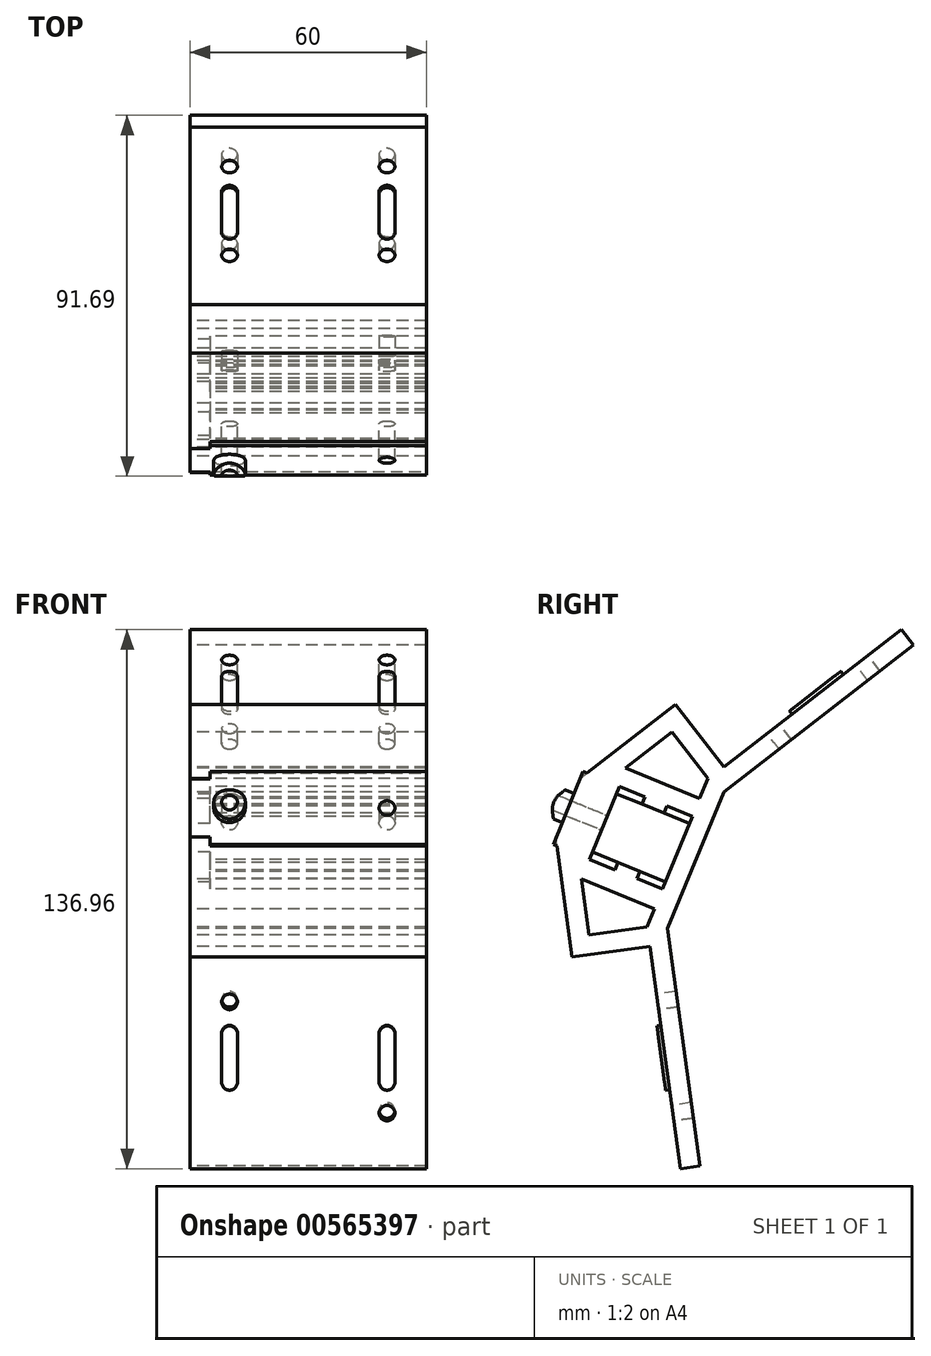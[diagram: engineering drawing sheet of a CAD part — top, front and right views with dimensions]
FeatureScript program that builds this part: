
annotation { "Feature Type Name" : "Feature", "Feature Type Description" : "" }
export const myFeature = defineFeature(function(context is Context, id is Id, definition is map)
    precondition{}
    {
        {
            var Q0;
            Q0=qCreatedBy(makeId("Right.planeOp"),FACE);
            var sketch = newSketch(context, id + "F0", { "sketchPlane" : qUnion([Q0])});
            skLineSegment(sketch, "E0", {"start": v(-33.6, 14.18) * mm, "end": v(-1.95, 38.65) * mm});
            skLineSegment(sketch, "E1", {"start": v(-1.95, 38.65) * mm, "end": v(10.28, 22.83) * mm});
            skLineSegment(sketch, "E2", {"start": v(-8.4, -22.77) * mm, "end": v(-28.23, -25.46) * mm});
            skLineSegment(sketch, "E3", {"start": v(-28.23, -25.46) * mm, "end": v(-33.6, 14.18) * mm});
            skLineSegment(sketch, "E4", {"start": v(10.28, 22.83) * mm, "end": v(55.37, 57.7) * mm});
            skLineSegment(sketch, "E5", {"start": v(55.37, 57.7) * mm, "end": v(58.43, 53.74) * mm});
            skLineSegment(sketch, "E6", {"start": v(58.43, 53.74) * mm, "end": v(10.28, 16.5) * mm});
            skLineSegment(sketch, "E7", {"start": v(10.28, 16.5) * mm, "end": v(-3.97, -18.27) * mm});
            skLineSegment(sketch, "E8", {"start": v(-3.97, -18.27) * mm, "end": v(4.2, -78.59) * mm});
            skLineSegment(sketch, "E9", {"start": v(4.2, -78.59) * mm, "end": v(-0.75, -79.26) * mm});
            skLineSegment(sketch, "E10", {"start": v(-0.75, -79.26) * mm, "end": v(-8.4, -22.77) * mm});
            skPoint(sketch, "E11", {"position": v(34.35, 35.12) * mm});
            skPoint(sketch, "E12", {"position": v(0.11, -48.43) * mm});
            skLineSegment(sketch, "E13", {"start": v(2.32, 10.27) * mm, "end": v(-16.19, 17.85) * mm});
            skLineSegment(sketch, "E14", {"start": v(-16.19, 17.85) * mm, "end": v(-23.77, -0.65) * mm});
            skLineSegment(sketch, "E15", {"start": v(-23.77, -0.65) * mm, "end": v(-5.26, -8.24) * mm});
            skLineSegment(sketch, "E16", {"start": v(-5.26, -8.24) * mm, "end": v(2.32, 10.27) * mm});
            skPoint(sketch, "E17", {"position": v(3.15, -0.88) * mm});
            skPoint(sketch, "E18", {"position": v(-1.47, 1.01) * mm});
            skLineSegment(sketch, "E19", {"start": v(3.15, -0.88) * mm, "end": v(-1.47, 1.01) * mm});
            skLineSegment(sketch, "E20", {"start": v(1.56, 8.42) * mm, "end": v(-16.94, 16) * mm});
            skLineSegment(sketch, "E21", {"start": v(-4.5, -6.39) * mm, "end": v(-23.01, 1.2) * mm});
            skLineSegment(sketch, "E22", {"start": v(-11.74, -5.58) * mm, "end": v(-10.98, -3.73) * mm});
            skLineSegment(sketch, "E23", {"start": v(-17.3, -3.3) * mm, "end": v(-16.53, -1.46) * mm});
            skLineSegment(sketch, "E24", {"start": v(-10.47, 13.35) * mm, "end": v(-9.7, 15.2) * mm});
            skPoint(sketch, "E25", {"position": v(-14.52, -4.45) * mm});
            skPoint(sketch, "E26", {"position": v(-6.93, 14.06) * mm});
            skLineSegment(sketch, "E27", {"start": v(-4.92, 11.07) * mm, "end": v(-4.16, 12.92) * mm});
            skLineSegment(sketch, "E28", {"start": v(-2.85, 31.63) * mm, "end": v(6.25, 19.86) * mm});
            skLineSegment(sketch, "E29", {"start": v(6.25, 19.86) * mm, "end": v(4.17, 14.8) * mm});
            skLineSegment(sketch, "E30", {"start": v(4.17, 14.8) * mm, "end": v(-14.65, 22.5) * mm});
            skLineSegment(sketch, "E31", {"start": v(-14.65, 22.5) * mm, "end": v(-2.85, 31.63) * mm});
            skLineSegment(sketch, "E32", {"start": v(-7.31, -13.24) * mm, "end": v(-9.2, -17.83) * mm});
            skLineSegment(sketch, "E33", {"start": v(-9.2, -17.83) * mm, "end": v(-23.94, -19.83) * mm});
            skLineSegment(sketch, "E34", {"start": v(-23.94, -19.83) * mm, "end": v(-25.87, -5.64) * mm});
            skPoint(sketch, "E34.endSnap0", {"position": v(-30.91, -5.64) * mm});
            skLineSegment(sketch, "E35", {"start": v(-25.87, -5.64) * mm, "end": v(-7.31, -13.24) * mm});
            skSolve(sketch);
        }
        {
            var Q0;
            Q0 = qSketchRegion(id + "F0", true);
            extrude(context, id + "F1", {"entities" : qUnion([Q0]), "depth" : 60 * mm, "offsetDistance" : 25 * mm});
        }
        {
            var Q0;
            {var subQ3=sQuery(id+"F0.wireOp",EDGE,"E24");Q0=makeQuery(id+"F0.imprint","IMPRINT",FACE,{"disambiguationData":[TD([[makeQuery(id+"F0.imprint","IMPRINT",EDGE,{"derivedFrom":subQ3}),1.0]])]});}
            var Q1;
            {var subQ3=sQuery(id+"F0.wireOp",EDGE,"E27");Q1=makeQuery(id+"F0.imprint","IMPRINT",FACE,{"disambiguationData":[TD([[makeQuery(id+"F0.imprint","IMPRINT",EDGE,{"derivedFrom":subQ3}),-1.0]])]});}
            var Q2;
            {var subQ3=sQuery(id+"F0.wireOp",EDGE,"E22");Q2=makeQuery(id+"F0.imprint","IMPRINT",FACE,{"disambiguationData":[TD([[makeQuery(id+"F0.imprint","IMPRINT",EDGE,{"derivedFrom":subQ3}),-1.0]])]});}
            var Q3;
            {var subQ5=sQuery(id+"F0.wireOp",EDGE,"E23");Q3=makeQuery(id+"F0.imprint","IMPRINT",FACE,{"disambiguationData":[TD([[makeQuery(id+"F0.imprint","IMPRINT",EDGE,{"derivedFrom":subQ5}),1.0]])]});}
            extrude(context, id + "F2", {"entities" : qUnion([Q0, Q1, Q2, Q3]), "operationType" : NewBodyOperationType.ADD, "depth" : 5 * mm, "offsetDistance" : 25 * mm});
        }
        {
            var Q0;
            {var subQ0=sQuery(id+"F0.wireOp",EDGE,"E22");Q0=makeQuery(id+"F0.imprint","IMPRINT",FACE,{"disambiguationData":[TD([[makeQuery(id+"F0.imprint","IMPRINT",EDGE,{"derivedFrom":subQ0}),1.0]])]});}
            var Q1;
            {var subQ0=sQuery(id+"F0.wireOp",EDGE,"E24");Q1=makeQuery(id+"F0.imprint","IMPRINT",FACE,{"disambiguationData":[TD([[makeQuery(id+"F0.imprint","IMPRINT",EDGE,{"derivedFrom":subQ0}),-1.0]])]});}
            extrude(context, id + "F3", {"entities" : qUnion([Q0, Q1]), "operationType" : NewBodyOperationType.ADD, "depth" : 60 * mm, "offsetDistance" : 25 * mm});
        }
        {
            var Q0;
            Q0=makeQuery(id+"F1.opExtrude","SWEPT_EDGE",EDGE,{"disambiguationData":[OSD([sQuery(id+"F0.wireOp",EDGE,"E0"),sQuery(id+"F0.wireOp",EDGE,"E3")])]});
            fillet(context, id + "F4", {"entities" : qUnion([Q0]), "radius" : 5 * mm, "tangentPropagation" : true, "allowEdgeOverflow" : false});
        }
        {
            var Q0;
            Q0=makeQuery(id+"F1.opExtrude","SWEPT_FACE",FACE,{"disambiguationData":[OSD([sQuery(id+"F0.wireOp",EDGE,"E4")])]});
            var sketch = newSketch(context, id + "F5", { "sketchPlane" : qUnion([Q0])});
            skCircle(sketch, "E36", {"center": v(50, 66.47) * mm, "radius": 2 * mm});
            skCircle(sketch, "E37", {"center": v(50, 37.97) * mm, "radius": 2 * mm});
            skCircle(sketch, "E38", {"center": v(10, 37.97) * mm, "radius": 2 * mm});
            skCircle(sketch, "E39", {"center": v(10, 66.47) * mm, "radius": 2 * mm});
            skLineSegment(sketch, "E40", {"start": v(48, 66.47) * mm, "end": v(48, 37.97) * mm});
            skLineSegment(sketch, "E41", {"start": v(12, 37.97) * mm, "end": v(12, 66.47) * mm});
            skLineSegment(sketch, "E42", {"start": v(52, 66.47) * mm, "end": v(52, 37.97) * mm});
            skLineSegment(sketch, "E43", {"start": v(8, 66.47) * mm, "end": v(8, 37.97) * mm});
            skCircle(sketch, "E44", {"center": v(50, 58.47) * mm, "radius": 2 * mm});
            skCircle(sketch, "E45", {"center": v(50, 45.97) * mm, "radius": 2 * mm});
            skCircle(sketch, "E46", {"center": v(10, 58.47) * mm, "radius": 2 * mm});
            skCircle(sketch, "E47", {"center": v(10, 45.97) * mm, "radius": 2 * mm});
            skSolve(sketch);
        }
        {
            var Q0;
            Q0=makeQuery(id+"F1.opExtrude","SWEPT_FACE",FACE,{"disambiguationData":[OSD([sQuery(id+"F0.wireOp",EDGE,"E10")])]});
            var sketch = newSketch(context, id + "F6", { "sketchPlane" : qUnion([Q0])});
            skCircle(sketch, "E48", {"center": v(10, -64.19) * mm, "radius": 2 * mm});
            skCircle(sketch, "E49", {"center": v(10, -35.69) * mm, "radius": 2 * mm});
            skCircle(sketch, "E50", {"center": v(50, -35.7) * mm, "radius": 2 * mm});
            skCircle(sketch, "E51", {"center": v(50, -64.18) * mm, "radius": 2 * mm});
            skLineSegment(sketch, "E52", {"start": v(12, -64.19) * mm, "end": v(12, -35.69) * mm});
            skLineSegment(sketch, "E53", {"start": v(8, -64.19) * mm, "end": v(8, -35.69) * mm});
            skCircle(sketch, "E54", {"center": v(10, -56.19) * mm, "radius": 2 * mm});
            skCircle(sketch, "E55", {"center": v(10, -43.69) * mm, "radius": 2 * mm});
            skLineSegment(sketch, "E56", {"start": v(48, -64.18) * mm, "end": v(48, -35.7) * mm});
            skLineSegment(sketch, "E57", {"start": v(52, -64.18) * mm, "end": v(52, -35.7) * mm});
            skCircle(sketch, "E58", {"center": v(50, -56.18) * mm, "radius": 2 * mm});
            skCircle(sketch, "E59", {"center": v(50, -43.7) * mm, "radius": 2 * mm});
            skSolve(sketch);
        }
        {
            var Q0;
            {var subQ0=sQuery(id+"F6.wireOp",EDGE,"E50");var subQ2=makeQuery(id+"F6.imprint","IMPRINT",VERTEX,{"derivedFrom":subQ0});Q0=makeQuery(id+"F6.imprint","IMPRINT",FACE,{"disambiguationData":[TD([[makeQuery(id+"F6.imprint","IMPRINT",EDGE,{"disambiguationData":[TD([[subQ2,1.0]])],"derivedFrom":subQ0}),1.0]])]});}
            var Q1;
            {var subQ0=sQuery(id+"F6.wireOp",EDGE,"E51");var subQ1=makeQuery(id+"F6.imprint","INTERSECT",VERTEX,{"derivedFrom":[subQ0,sQuery(id+"F6.wireOp",EDGE,"E56")]});Q1=makeQuery(id+"F6.imprint","IMPRINT",FACE,{"disambiguationData":[TD([[makeQuery(id+"F6.imprint","IMPRINT",EDGE,{"disambiguationData":[TD([[subQ1,1.0]])],"derivedFrom":subQ0}),1.0]])]});}
            var Q2;
            {var subQ0=sQuery(id+"F6.wireOp",EDGE,"E49");var subQ1=makeQuery(id+"F6.imprint","INTERSECT",VERTEX,{"derivedFrom":[subQ0,sQuery(id+"F6.wireOp",EDGE,"E52")]});Q2=makeQuery(id+"F6.imprint","IMPRINT",FACE,{"disambiguationData":[TD([[makeQuery(id+"F6.imprint","IMPRINT",EDGE,{"disambiguationData":[TD([[subQ1,1.0]])],"derivedFrom":subQ0}),1.0]])]});}
            var Q3;
            {var subQ0=sQuery(id+"F6.wireOp",EDGE,"E48");var subQ2=makeQuery(id+"F6.imprint","IMPRINT",VERTEX,{"derivedFrom":subQ0});Q3=makeQuery(id+"F6.imprint","IMPRINT",FACE,{"disambiguationData":[TD([[makeQuery(id+"F6.imprint","IMPRINT",EDGE,{"disambiguationData":[TD([[subQ2,1.0]])],"derivedFrom":subQ0}),1.0]])]});}
            extrude(context, id + "F7", {"entities" : qUnion([Q0, Q1, Q2, Q3]), "operationType" : NewBodyOperationType.REMOVE, "oppositeDirection" : true, "depth" : 5 * mm, "offsetDistance" : 25 * mm});
        }
        {
            var Q0;
            {var subQ0=sQuery(id+"F5.wireOp",EDGE,"E36");var subQ1=makeQuery(id+"F5.imprint","INTERSECT",VERTEX,{"derivedFrom":[subQ0,sQuery(id+"F5.wireOp",EDGE,"E40")]});Q0=makeQuery(id+"F5.imprint","IMPRINT",FACE,{"disambiguationData":[TD([[makeQuery(id+"F5.imprint","IMPRINT",EDGE,{"disambiguationData":[TD([[subQ1,1.0]])],"derivedFrom":subQ0}),1.0]])]});}
            var Q1;
            {var subQ0=sQuery(id+"F5.wireOp",EDGE,"E37");var subQ1=makeQuery(id+"F5.imprint","INTERSECT",VERTEX,{"derivedFrom":[subQ0,sQuery(id+"F5.wireOp",EDGE,"E40")]});Q1=makeQuery(id+"F5.imprint","IMPRINT",FACE,{"disambiguationData":[TD([[makeQuery(id+"F5.imprint","IMPRINT",EDGE,{"disambiguationData":[TD([[subQ1,1.0]])],"derivedFrom":subQ0}),1.0]])]});}
            var Q2;
            {var subQ0=sQuery(id+"F5.wireOp",EDGE,"E38");var subQ1=makeQuery(id+"F5.imprint","INTERSECT",VERTEX,{"derivedFrom":[subQ0,sQuery(id+"F5.wireOp",EDGE,"E41")]});Q2=makeQuery(id+"F5.imprint","IMPRINT",FACE,{"disambiguationData":[TD([[makeQuery(id+"F5.imprint","IMPRINT",EDGE,{"disambiguationData":[TD([[subQ1,-1.0]])],"derivedFrom":subQ0}),1.0]])]});}
            var Q3;
            {var subQ0=sQuery(id+"F5.wireOp",EDGE,"E39");var subQ1=makeQuery(id+"F5.imprint","INTERSECT",VERTEX,{"derivedFrom":[subQ0,sQuery(id+"F5.wireOp",EDGE,"E41")]});Q3=makeQuery(id+"F5.imprint","IMPRINT",FACE,{"disambiguationData":[TD([[makeQuery(id+"F5.imprint","IMPRINT",EDGE,{"disambiguationData":[TD([[subQ1,-1.0]])],"derivedFrom":subQ0}),1.0]])]});}
            extrude(context, id + "F8", {"entities" : qUnion([Q0, Q1, Q2, Q3]), "operationType" : NewBodyOperationType.REMOVE, "oppositeDirection" : true, "depth" : 5 * mm, "offsetDistance" : 25 * mm});
        }
        {
            var Q0;
            {var subQ0=sQuery(id+"F5.wireOp",EDGE,"E44");var subQ1=makeQuery(id+"F5.imprint","INTERSECT",VERTEX,{"derivedFrom":[sQuery(id+"F5.wireOp",EDGE,"E40"),subQ0]});Q0=makeQuery(id+"F5.imprint","IMPRINT",FACE,{"disambiguationData":[TD([[makeQuery(id+"F5.imprint","IMPRINT",EDGE,{"disambiguationData":[TD([[subQ1,1.0]])],"derivedFrom":subQ0}),1.0]])]});}
            var Q1;
            {var subQ0=sQuery(id+"F5.wireOp",EDGE,"E44");var subQ1=sQuery(id+"F5.wireOp",EDGE,"E40");var subQ2=makeQuery(id+"F5.imprint","INTERSECT",VERTEX,{"derivedFrom":[subQ1,subQ0]});Q1=makeQuery(id+"F5.imprint","IMPRINT",FACE,{"disambiguationData":[TD([[makeQuery(id+"F5.imprint","IMPRINT",EDGE,{"disambiguationData":[TD([[subQ2,-1.0]])],"derivedFrom":subQ1}),1.0]])]});}
            var Q2;
            {var subQ0=sQuery(id+"F5.wireOp",EDGE,"E45");var subQ1=makeQuery(id+"F5.imprint","INTERSECT",VERTEX,{"derivedFrom":[sQuery(id+"F5.wireOp",EDGE,"E40"),subQ0]});Q2=makeQuery(id+"F5.imprint","IMPRINT",FACE,{"disambiguationData":[TD([[makeQuery(id+"F5.imprint","IMPRINT",EDGE,{"disambiguationData":[TD([[subQ1,1.0]])],"derivedFrom":subQ0}),1.0]])]});}
            var Q3;
            {var subQ0=sQuery(id+"F5.wireOp",EDGE,"E46");var subQ1=makeQuery(id+"F5.imprint","INTERSECT",VERTEX,{"derivedFrom":[sQuery(id+"F5.wireOp",EDGE,"E41"),subQ0]});Q3=makeQuery(id+"F5.imprint","IMPRINT",FACE,{"disambiguationData":[TD([[makeQuery(id+"F5.imprint","IMPRINT",EDGE,{"disambiguationData":[TD([[subQ1,-1.0]])],"derivedFrom":subQ0}),1.0]])]});}
            var Q4;
            {var subQ0=sQuery(id+"F5.wireOp",EDGE,"E47");var subQ1=sQuery(id+"F5.wireOp",EDGE,"E41");var subQ2=makeQuery(id+"F5.imprint","INTERSECT",VERTEX,{"derivedFrom":[subQ1,subQ0]});Q4=makeQuery(id+"F5.imprint","IMPRINT",FACE,{"disambiguationData":[TD([[makeQuery(id+"F5.imprint","IMPRINT",EDGE,{"disambiguationData":[TD([[subQ2,-1.0]])],"derivedFrom":subQ1}),1.0]])]});}
            var Q5;
            {var subQ0=sQuery(id+"F5.wireOp",EDGE,"E47");var subQ1=makeQuery(id+"F5.imprint","INTERSECT",VERTEX,{"derivedFrom":[sQuery(id+"F5.wireOp",EDGE,"E41"),subQ0]});Q5=makeQuery(id+"F5.imprint","IMPRINT",FACE,{"disambiguationData":[TD([[makeQuery(id+"F5.imprint","IMPRINT",EDGE,{"disambiguationData":[TD([[subQ1,-1.0]])],"derivedFrom":subQ0}),1.0]])]});}
            extrude(context, id + "F9", {"entities" : qUnion([Q0, Q1, Q2, Q3, Q4, Q5]), "operationType" : NewBodyOperationType.ADD, "depth" : 1 * mm, "offsetDistance" : 25 * mm});
        }
        {
            var Q0;
            {var subQ0=sQuery(id+"F6.wireOp",EDGE,"E59");var subQ1=makeQuery(id+"F6.imprint","INTERSECT",VERTEX,{"derivedFrom":[sQuery(id+"F6.wireOp",EDGE,"E56"),subQ0]});Q0=makeQuery(id+"F6.imprint","IMPRINT",FACE,{"disambiguationData":[TD([[makeQuery(id+"F6.imprint","IMPRINT",EDGE,{"disambiguationData":[TD([[subQ1,1.0]])],"derivedFrom":subQ0}),1.0]])]});}
            var Q1;
            {var subQ0=sQuery(id+"F6.wireOp",EDGE,"E58");var subQ1=sQuery(id+"F6.wireOp",EDGE,"E56");var subQ2=makeQuery(id+"F6.imprint","INTERSECT",VERTEX,{"derivedFrom":[subQ1,subQ0]});Q1=makeQuery(id+"F6.imprint","IMPRINT",FACE,{"disambiguationData":[TD([[makeQuery(id+"F6.imprint","IMPRINT",EDGE,{"disambiguationData":[TD([[subQ2,-1.0]])],"derivedFrom":subQ1}),-1.0]])]});}
            var Q2;
            {var subQ0=sQuery(id+"F6.wireOp",EDGE,"E58");var subQ1=makeQuery(id+"F6.imprint","INTERSECT",VERTEX,{"derivedFrom":[sQuery(id+"F6.wireOp",EDGE,"E56"),subQ0]});Q2=makeQuery(id+"F6.imprint","IMPRINT",FACE,{"disambiguationData":[TD([[makeQuery(id+"F6.imprint","IMPRINT",EDGE,{"disambiguationData":[TD([[subQ1,1.0]])],"derivedFrom":subQ0}),1.0]])]});}
            var Q3;
            {var subQ0=sQuery(id+"F6.wireOp",EDGE,"E55");var subQ1=makeQuery(id+"F6.imprint","INTERSECT",VERTEX,{"derivedFrom":[sQuery(id+"F6.wireOp",EDGE,"E52"),subQ0]});Q3=makeQuery(id+"F6.imprint","IMPRINT",FACE,{"disambiguationData":[TD([[makeQuery(id+"F6.imprint","IMPRINT",EDGE,{"disambiguationData":[TD([[subQ1,-1.0]])],"derivedFrom":subQ0}),1.0]])]});}
            var Q4;
            {var subQ0=sQuery(id+"F6.wireOp",EDGE,"E54");var subQ1=sQuery(id+"F6.wireOp",EDGE,"E52");var subQ2=makeQuery(id+"F6.imprint","INTERSECT",VERTEX,{"derivedFrom":[subQ1,subQ0]});Q4=makeQuery(id+"F6.imprint","IMPRINT",FACE,{"disambiguationData":[TD([[makeQuery(id+"F6.imprint","IMPRINT",EDGE,{"disambiguationData":[TD([[subQ2,-1.0]])],"derivedFrom":subQ1}),1.0]])]});}
            var Q5;
            {var subQ0=sQuery(id+"F6.wireOp",EDGE,"E54");var subQ1=makeQuery(id+"F6.imprint","INTERSECT",VERTEX,{"derivedFrom":[sQuery(id+"F6.wireOp",EDGE,"E52"),subQ0]});Q5=makeQuery(id+"F6.imprint","IMPRINT",FACE,{"disambiguationData":[TD([[makeQuery(id+"F6.imprint","IMPRINT",EDGE,{"disambiguationData":[TD([[subQ1,-1.0]])],"derivedFrom":subQ0}),1.0]])]});}
            extrude(context, id + "F10", {"entities" : qUnion([Q0, Q1, Q2, Q3, Q4, Q5]), "operationType" : NewBodyOperationType.ADD, "depth" : 1 * mm, "offsetDistance" : 25 * mm});
        }
        {
            var Q0;
            Q0=makeQuery(id+"F1.opExtrude","SWEPT_FACE",FACE,{"disambiguationData":[OSD([sQuery(id+"F0.wireOp",EDGE,"E14")])]});
            var sketch = newSketch(context, id + "F11", { "sketchPlane" : qUnion([Q0])});
            skLineSegment(sketch, "E60", {"start": v(0, 0.38) * mm, "end": v(-60, 0.38) * mm});
            skCircle(sketch, "E61", {"center": v(-50, 0.38) * mm, "radius": 2 * mm});
            skCircle(sketch, "E62", {"center": v(-50, 0.38) * mm, "radius": 4 * mm});
            skCircle(sketch, "E63", {"center": v(-10, 0.38) * mm, "radius": 2 * mm});
            skCircle(sketch, "E64", {"center": v(-10, 0.38) * mm, "radius": 4 * mm});
            skSolve(sketch);
        }
        {
            var Q0;
            {var subQ0=sQuery(id+"F11.wireOp",EDGE,"E63");var subQ1=sQuery(id+"F11.wireOp",EDGE,"E60");var subQ2=makeQuery(id+"F11.imprint","INTERSECT",VERTEX,{"disambiguationData":[OD(0.0)],"derivedFrom":[subQ1,subQ0]});Q0=makeQuery(id+"F11.imprint","IMPRINT",FACE,{"disambiguationData":[TD([[makeQuery(id+"F11.imprint","IMPRINT",EDGE,{"disambiguationData":[TD([[subQ2,-1.0]])],"derivedFrom":subQ1}),-1.0]])]});}
            var Q1;
            {var subQ0=sQuery(id+"F11.wireOp",EDGE,"E61");var subQ1=sQuery(id+"F11.wireOp",EDGE,"E60");var subQ2=makeQuery(id+"F11.imprint","INTERSECT",VERTEX,{"disambiguationData":[OD(0.0)],"derivedFrom":[subQ1,subQ0]});Q1=makeQuery(id+"F11.imprint","IMPRINT",FACE,{"disambiguationData":[TD([[makeQuery(id+"F11.imprint","IMPRINT",EDGE,{"disambiguationData":[TD([[subQ2,-1.0]])],"derivedFrom":subQ1}),-1.0]])]});}
            var Q2;
            {var subQ0=sQuery(id+"F11.wireOp",EDGE,"E61");var subQ1=sQuery(id+"F11.wireOp",EDGE,"E60");var subQ2=makeQuery(id+"F11.imprint","INTERSECT",VERTEX,{"disambiguationData":[OD(0.0)],"derivedFrom":[subQ1,subQ0]});Q2=makeQuery(id+"F11.imprint","IMPRINT",FACE,{"disambiguationData":[TD([[makeQuery(id+"F11.imprint","IMPRINT",EDGE,{"disambiguationData":[TD([[subQ2,-1.0]])],"derivedFrom":subQ1}),1.0]])]});}
            var Q3;
            {var subQ0=sQuery(id+"F11.wireOp",EDGE,"E63");var subQ1=sQuery(id+"F11.wireOp",EDGE,"E60");var subQ2=makeQuery(id+"F11.imprint","INTERSECT",VERTEX,{"disambiguationData":[OD(0.0)],"derivedFrom":[subQ1,subQ0]});Q3=makeQuery(id+"F11.imprint","IMPRINT",FACE,{"disambiguationData":[TD([[makeQuery(id+"F11.imprint","IMPRINT",EDGE,{"disambiguationData":[TD([[subQ2,-1.0]])],"derivedFrom":subQ1}),1.0]])]});}
            extrude(context, id + "F12", {"entities" : qUnion([Q0, Q1, Q2, Q3]), "operationType" : NewBodyOperationType.REMOVE, "oppositeDirection" : true, "depth" : 25 * mm, "offsetDistance" : 25 * mm});
        }
        {
            var Q0;
            {var subQ0=sQuery(id+"F11.wireOp",EDGE,"E62");var subQ1=sQuery(id+"F11.wireOp",EDGE,"E60");var subQ2=makeQuery(id+"F11.imprint","INTERSECT",VERTEX,{"disambiguationData":[OD(0.0)],"derivedFrom":[subQ1,subQ0]});Q0=makeQuery(id+"F11.imprint","IMPRINT",FACE,{"disambiguationData":[TD([[makeQuery(id+"F11.imprint","IMPRINT",EDGE,{"disambiguationData":[TD([[subQ2,-1.0]])],"derivedFrom":subQ1}),-1.0]])]});}
            var Q1;
            {var subQ0=sQuery(id+"F11.wireOp",EDGE,"E62");var subQ1=sQuery(id+"F11.wireOp",EDGE,"E60");var subQ2=makeQuery(id+"F11.imprint","INTERSECT",VERTEX,{"disambiguationData":[OD(0.0)],"derivedFrom":[subQ1,subQ0]});Q1=makeQuery(id+"F11.imprint","IMPRINT",FACE,{"disambiguationData":[TD([[makeQuery(id+"F11.imprint","IMPRINT",EDGE,{"disambiguationData":[TD([[subQ2,-1.0]])],"derivedFrom":subQ1}),1.0]])]});}
            var Q2;
            {var subQ0=sQuery(id+"F11.wireOp",EDGE,"E64");var subQ1=sQuery(id+"F11.wireOp",EDGE,"E60");var subQ2=makeQuery(id+"F11.imprint","INTERSECT",VERTEX,{"disambiguationData":[OD(0.0)],"derivedFrom":[subQ1,subQ0]});Q2=makeQuery(id+"F11.imprint","IMPRINT",FACE,{"disambiguationData":[TD([[makeQuery(id+"F11.imprint","IMPRINT",EDGE,{"disambiguationData":[TD([[subQ2,-1.0]])],"derivedFrom":subQ1}),1.0]])]});}
            var Q3;
            {var subQ0=sQuery(id+"F11.wireOp",EDGE,"E64");var subQ1=sQuery(id+"F11.wireOp",EDGE,"E60");var subQ2=makeQuery(id+"F11.imprint","INTERSECT",VERTEX,{"disambiguationData":[OD(0.0)],"derivedFrom":[subQ1,subQ0]});Q3=makeQuery(id+"F11.imprint","IMPRINT",FACE,{"disambiguationData":[TD([[makeQuery(id+"F11.imprint","IMPRINT",EDGE,{"disambiguationData":[TD([[subQ2,-1.0]])],"derivedFrom":subQ1}),-1.0]])]});}
            extrude(context, id + "F13", {"entities" : qUnion([Q0, Q1, Q2, Q3]), "operationType" : NewBodyOperationType.ADD, "oppositeDirection" : true, "depth" : 20 * mm, "offsetDistance" : 25 * mm});
        }
        {
            var Q0;
            Q0=makeQuery(id+"F13.opExtrude","CAP_FACE",FACE,{"disambiguationData":[OSD([sQuery(id+"F11.wireOp",EDGE,"E63"),sQuery(id+"F11.wireOp",EDGE,"E64")])],"isStart":false});
            var Q1;
            Q1=makeQuery(id+"F13.opExtrude","CAP_FACE",FACE,{"disambiguationData":[OSD([sQuery(id+"F11.wireOp",EDGE,"E61"),sQuery(id+"F11.wireOp",EDGE,"E62")])],"isStart":false});
            extrude(context, id + "F14", {"entities" : qUnion([Q0, Q1]), "operationType" : NewBodyOperationType.REMOVE, "oppositeDirection" : true, "depth" : 10 * mm, "offsetDistance" : 25 * mm});
        }
    });
